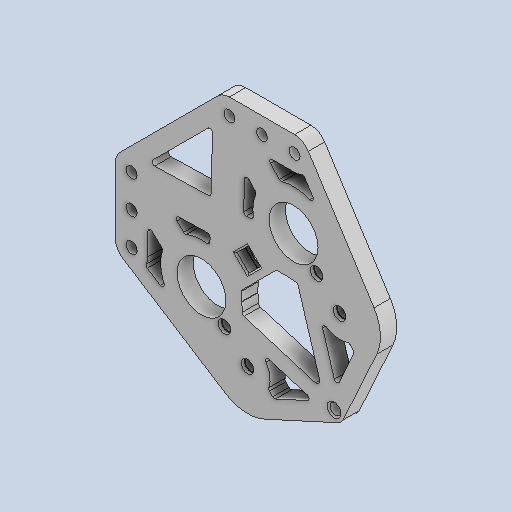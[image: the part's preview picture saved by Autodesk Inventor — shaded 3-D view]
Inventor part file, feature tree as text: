
AUTODESK INVENTOR PART (.ipt)
format: ipt  version: 2022 (Build 260153000, 153)  size: 789,504 bytes
history: native  units: in
note: dims shown in document units (in); Inventor stores cm internally (conversion verified against a paired STEP export)
features: extrude x5, sketch x5, other x4, projected_geometry x3, chamfer x2, reference x2, fillet x1
ambient origin geometry x8: Origin, YZ Plane, XZ Plane, XY Plane, X Axis, Y Axis, Z Axis, Center Point
bodies: Solid1 (feature_tree)
feature tree (22):
  extrude  "Extrusion1"  Depth=0.25in TaperAngle=0.0deg
  extrude  "Extrusion2"  Depth=0.05in
  extrude  "Extrusion3"  Depth=0.5in
  fillet  "Fillet1"  Radius=0.5in
  extrude  "Extrusion4"  Depth=0.25in
  extrude  "Extrusion5"  Depth=0.5in
  chamfer  "Chamfer1"  Distance=0.5in
  chamfer  "Chamfer2"  Angle=45.0deg  [1 undecoded]
  sketch  "Sketch1"  dims[d9=0.75in d11=0.25in d12=0.0in]
  reference  "Reference1"
  sketch  "Sketch2"  dims[d14=0.05in d15=0.0in d16=0.1679in]
  projected_geometry  "Projected Loop1"
  projected_geometry  "Projected Loop2"
  sketch  "Sketch3"  dims[d17=1.1811in d19=0.5in d20=0.3937in d22=1.0in d26=0.1938in d28=0.5in]
  projected_geometry  "Projected Loop3"
  sketch  "Sketch4"  dims[d29=0.25in d30=0.25in]
  reference  "Reference2"
  sketch  "Sketch5"  dims[d31=0.25in d33=0.5in d34=0.5in d35=45.0deg d36=0.25in d37=45.0deg d38=0.25in d39=0.5in d40=0.5in d41=0.25in d42=0.25in d43=0.5in d44=0.5in d45=0.0in d46=0.0in d47=0.0394in d48=0.261in d49=1.0in d50=0.0in d51=0.3957in d52=0.0787in d53=0.0in d54=0.0236in d55=0.125in d56=45.0deg d57=0.1679in d58=0.0236in d59=0.125in d60=45.0deg d61=0.1679in d62=0.1679in]
  other  "<userpath>\Documents\CAD\guardSwerve1\Assembly1.iam"
  other  "Assembly1.iam"
  other  "uppermidblock:1"
  other  "Undercarriage:1"
note: 1 required parameter value undecoded (feature->parameter linkage not recoverable at this tier; creation-order binding heuristic only, values carry confidence <= 0.55)
